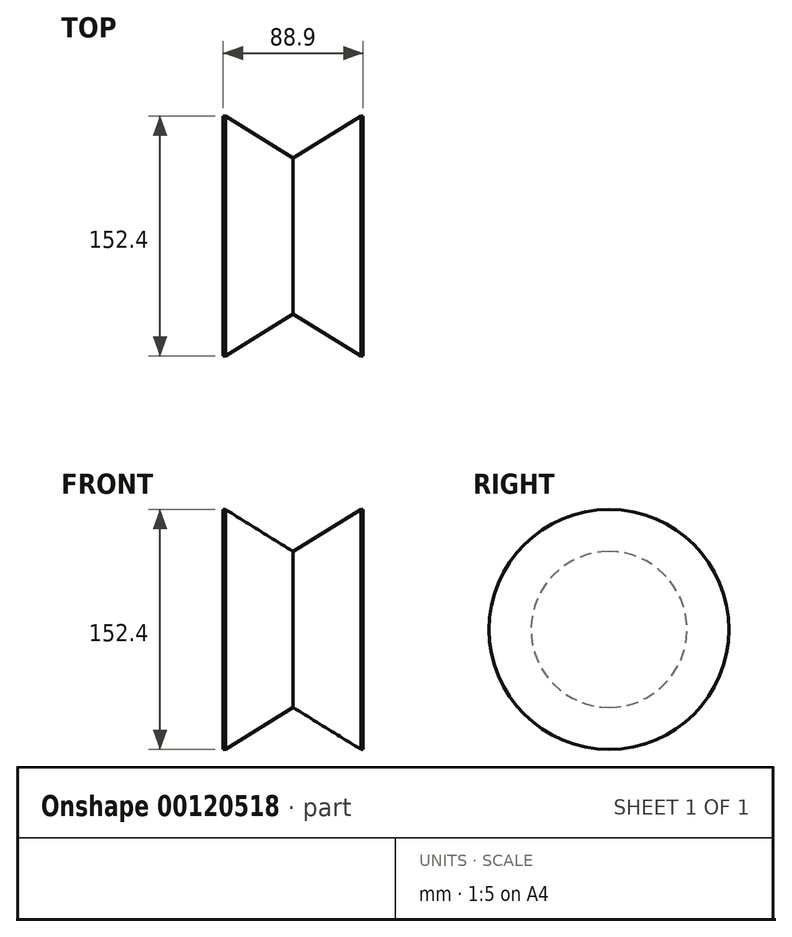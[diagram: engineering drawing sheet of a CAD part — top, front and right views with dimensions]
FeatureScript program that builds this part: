
annotation { "Feature Type Name" : "Feature", "Feature Type Description" : "" }
export const myFeature = defineFeature(function(context is Context, id is Id, definition is map)
    precondition{}
    {
        {
            var Q0;
            Q0=qCreatedBy(makeId("Right.planeOp"),FACE);
            var sketch = newSketch(context, id + "F0", { "sketchPlane" : qUnion([Q0])});
            skCircle(sketch, "E0", {"center": v(0, 0) * mm, "radius": 76.2 * mm});
            skSolve(sketch);
        }
        {
            var Q0;
            Q0=makeQuery(id+"F0.imprint","IMPRINT",FACE,{"disambiguationData":[TD([[makeQuery(id+"F0.imprint","IMPRINT",EDGE,{"derivedFrom":sQuery(id+"F0.wireOp",EDGE,"E0")}),1.0]])]});
            extrude(context, id + "F1", {"entities" : qUnion([Q0]), "depth" : 44.45 * mm, "hasSecondDirection" : true, "secondDirectionOppositeDirection" : true, "secondDirectionDepth" : 44.45 * mm});
        }
        {
            var Q0;
            Q0=qCreatedBy(makeId("Front.planeOp"),FACE);
            var sketch = newSketch(context, id + "F2", { "sketchPlane" : qUnion([Q0])});
            skLineSegment(sketch, "E1", {"start": v(0, 76.34) * mm, "end": v(43.19, 76.34) * mm});
            skLineSegment(sketch, "E2", {"start": v(43.19, 76.34) * mm, "end": v(0, 49.5) * mm});
            skLineSegment(sketch, "E3.MirrorCS", {"start": v(-43.19, 76.34) * mm, "end": v(0, 49.5) * mm});
            skLineSegment(sketch, "E4", {"start": v(-43.19, 76.34) * mm, "end": v(0, 76.34) * mm});
            skLineSegment(sketch, "E5", {"start": v(44.12, 0) * mm, "end": v(-58.31, 0) * mm});
            skSolve(sketch);
        }
        {
            var Q0;
            Q0 = qSketchRegion(id + "F2", true);
            var Q1;
            Q1=sQuery(id+"F2.wireOp",EDGE,"E5");
            revolve(context, id + "F3", {"operationType" : NewBodyOperationType.REMOVE, "entities" : qUnion([Q0]), "axis" : qUnion([Q1]), "revolveType" : RevolveType.FULL, "oppositeDirection" : true});
        }
    });
